# Revit family: Emergency_Equipment-Tepid-Swing_Down_Eye_Face_Wash-S2550
name_source: partatom
category: Plumbing Fixtures
revit_build: Autodesk Revit Architecture 2016 (Build: 20150220_1215(x64)
units: mm (PartAtom-declared; Revit-internal decimal feet)

## family parameters
Always vertical = No
Cut with Voids When Loaded = No
OmniClass Number = 23.45.05.14.24
OmniClass Title = Eye Wash Fountains
Part Type = Normal
Room Calculation Point = No
Round Connector Dimension = Use Diameter
Shared = No
Work Plane-Based = Yes

## types (2) — shared parameters
CW Connection = Yes
Default Elevation = 4' - 0"
Description = Swing Down Eyewash
Dimension Disclaimer = Dimensions are ±0.50”. Design and specifications are subject to change without notice.
HW Connection = Yes
Height = 1' - 2 11/16"
Length = 1' - 3"
Manufacturer = Stingray Systems
Pipe Finish = Metal - Stingray - Stainless Steel SS
Product Documentation Link = http://www.tepid.com
Product Name = Wall Mounted Swing Down Eyewash
Product Page URL = http://www.tepid.com
Supply Connection = 1"
URL = www.tepid.com
Vent Connection = No
Version = 2016-v1.0a
Waste Connection = No
Width = 0' - 4 5/16"

## per-type parameters (varying)
| type | Filter |
| S2550-NP-NFT | No |
| S2550-NP-FLT | Yes |

note: column(s) folded — value = type name in every type: Model

## geometry (parser evidence)
native form markers: Sweep x5
no freeform markers — native parametric forms only
